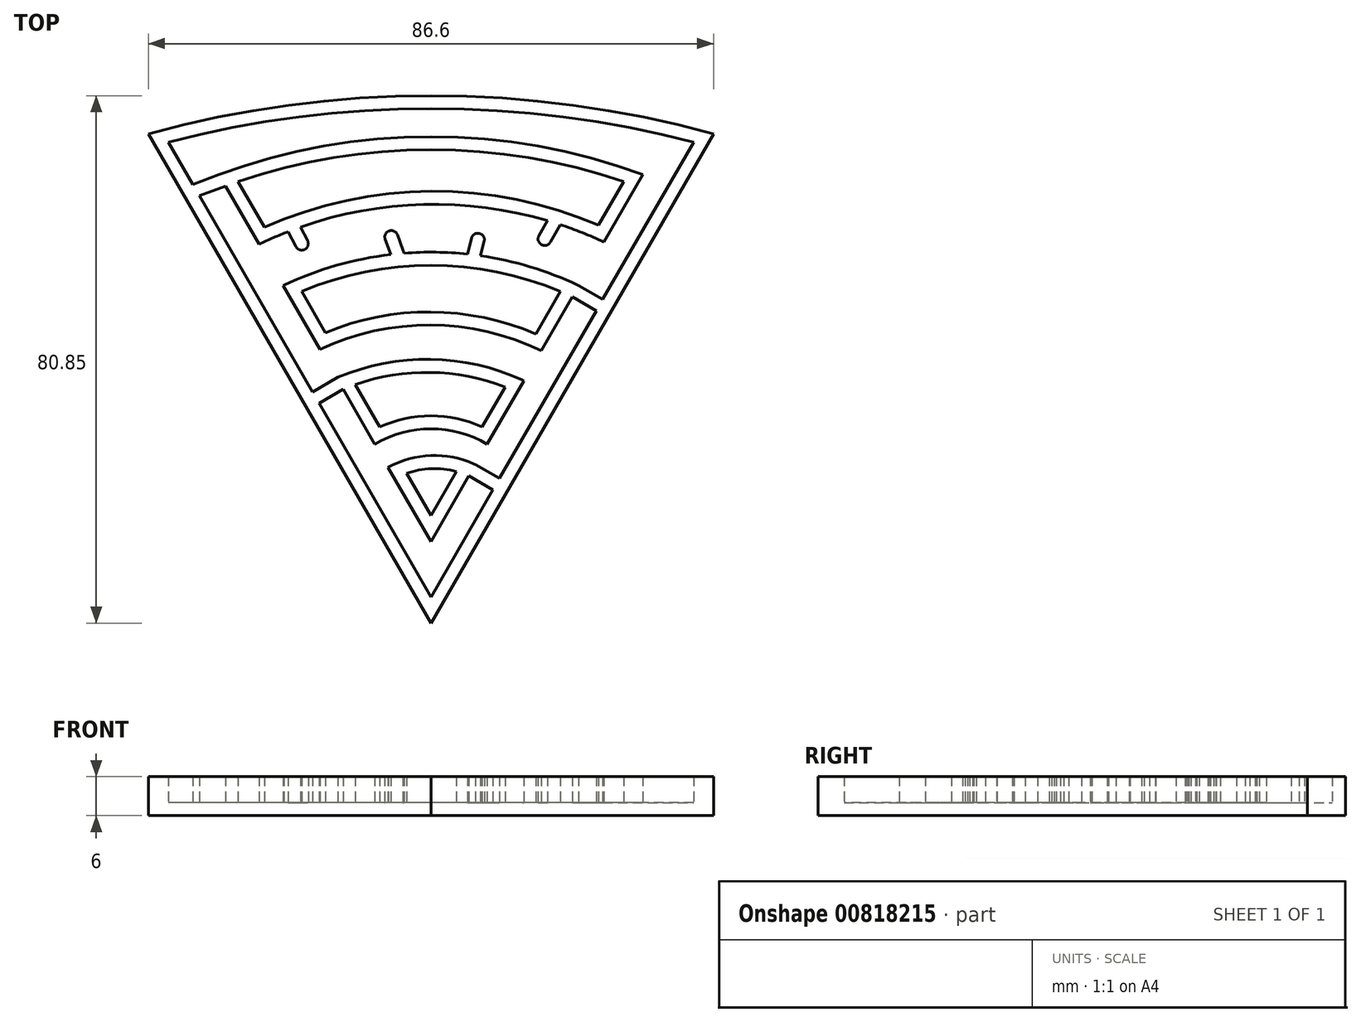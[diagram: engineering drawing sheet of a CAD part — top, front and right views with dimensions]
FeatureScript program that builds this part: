
annotation { "Feature Type Name" : "Feature", "Feature Type Description" : "" }
export const myFeature = defineFeature(function(context is Context, id is Id, definition is map)
    precondition{}
    {
        {
            var Q0;
            Q0=qCreatedBy(makeId("Top.planeOp"),FACE);
            var sketch = newSketch(context, id + "F0", { "sketchPlane" : qUnion([Q0])});
            skLineSegment(sketch, "E0.0", {"start": v(0, -50) * mm, "end": v(-43.3, 25) * mm});
            skLineSegment(sketch, "E0.2", {"start": v(43.3, 25) * mm, "end": v(0, -50) * mm});
            skLineSegment(sketch, "E1.0", {"start": v(0, -46) * mm, "end": v(-17.15, -16.3) * mm});
            skLineSegment(sketch, "E1.1", {"start": v(39.84, 23) * mm, "end": v(26.33, -0.39) * mm});
            skLineSegment(sketch, "E2.0", {"start": v(0, -37.5) * mm, "end": v(-6.57, -26.12) * mm});
            skLineSegment(sketch, "E2.2", {"start": v(32.48, 18.75) * mm, "end": v(26.51, 8.42) * mm});
            skArc(sketch, "E3", {"start": v(26.51, 8.42) * mm, "mid": v(23.2, 9.85) * mm, "end": v(19.82, 11.08) * mm});
            skArc(sketch, "E4.0", {"start": v(25.69, 10.99) * mm, "mid": v(0.06, 16.2) * mm, "end": v(-25.5, 10.67) * mm});
            skArc(sketch, "E5", {"start": v(19.82, 0.82) * mm, "mid": v(0, 4.86) * mm, "end": v(-19.82, 0.82) * mm});
            skArc(sketch, "E6.0", {"start": v(22.5, 1.8) * mm, "mid": v(15.21, 4.62) * mm, "end": v(7.58, 6.32) * mm});
            skLineSegment(sketch, "E7", {"start": v(22.5, 1.8) * mm, "end": v(22.65, 1.74) * mm});
            skLineSegment(sketch, "E8.trimOffspring", {"start": v(21.65, 0) * mm, "end": v(16.89, -8.25) * mm});
            skLineSegment(sketch, "E9", {"start": v(-22.5, 1.8) * mm, "end": v(-22.65, 1.73) * mm});
            skLineSegment(sketch, "E10.trimOffspring", {"start": v(-26.32, 8.08) * mm, "end": v(-31.46, 17) * mm});
            skArc(sketch, "E11", {"start": v(16.89, -8.25) * mm, "mid": v(-0.04, -4.3) * mm, "end": v(-17.02, -8.02) * mm});
            skArc(sketch, "E12.0", {"start": v(16.07, -5.67) * mm, "mid": v(-0.04, -2.3) * mm, "end": v(-16.18, -5.47) * mm});
            skArc(sketch, "E13", {"start": v(11.38, -13.8) * mm, "mid": v(-0.07, -11.57) * mm, "end": v(-11.59, -13.43) * mm});
            skArc(sketch, "E14.0", {"start": v(14.07, -12.75) * mm, "mid": v(-0.05, -9.57) * mm, "end": v(-14.25, -12.3) * mm});
            skLineSegment(sketch, "E15", {"start": v(14.07, -12.75) * mm, "end": v(14.24, -12.83) * mm});
            skLineSegment(sketch, "E16.trimOffspring", {"start": v(14.24, -12.83) * mm, "end": v(8.63, -22.56) * mm});
            skArc(sketch, "E17", {"start": v(8.63, -22.56) * mm, "mid": v(0, -20.22) * mm, "end": v(-8.6, -22.6) * mm});
            skArc(sketch, "E18", {"start": v(3.9, -26.75) * mm, "mid": v(0.06, -26.32) * mm, "end": v(-3.73, -27.04) * mm});
            skArc(sketch, "E19.0", {"start": v(9.64, -20.84) * mm, "mid": v(9.63, -20.83) * mm, "end": v(9.63, -20.83) * mm});
            skArc(sketch, "E20.0", {"start": v(6.63, -25.6) * mm, "mid": v(0, -24.32) * mm, "end": v(-6.52, -26.09) * mm});
            skLineSegment(sketch, "E21.trimOffspring", {"start": v(-17.02, -8.02) * mm, "end": v(-22.65, 1.73) * mm});
            skLineSegment(sketch, "E22", {"start": v(-6.52, -26.09) * mm, "end": v(-6.57, -26.12) * mm});
            skLineSegment(sketch, "E23", {"start": v(6.63, -25.6) * mm, "end": v(6.82, -25.7) * mm});
            skLineSegment(sketch, "E24.trimOffspring", {"start": v(5.82, -27.42) * mm, "end": v(0, -37.5) * mm});
            skLineSegment(sketch, "E25.trimOffspring", {"start": v(-8.6, -22.6) * mm, "end": v(-13.47, -14.17) * mm});
            skArc(sketch, "E26", {"start": v(43.3, 25) * mm, "mid": v(0, 30.85) * mm, "end": v(-43.3, 25) * mm});
            skArc(sketch, "E27", {"start": v(32.48, 18.75) * mm, "mid": v(0, 24.56) * mm, "end": v(-32.48, 18.75) * mm});
            skArc(sketch, "E28.0", {"start": v(40.26, 23.74) * mm, "mid": v(0, 28.85) * mm, "end": v(-40.26, 23.74) * mm});
            skLineSegment(sketch, "E29", {"start": v(-39.84, 23) * mm, "end": v(-40.26, 23.74) * mm});
            skLineSegment(sketch, "E30", {"start": v(39.84, 23) * mm, "end": v(40.26, 23.74) * mm});
            skLineSegment(sketch, "E31.0", {"start": v(0, -33.5) * mm, "end": v(-3.73, -27.04) * mm});
            skLineSegment(sketch, "E32.trimOffspring", {"start": v(3.9, -26.75) * mm, "end": v(0, -33.5) * mm});
            skLineSegment(sketch, "E33.0", {"start": v(-25.5, 10.67) * mm, "end": v(-29.54, 17.67) * mm});
            skLineSegment(sketch, "E34.0", {"start": v(19.82, 0.82) * mm, "end": v(16.07, -5.67) * mm});
            skLineSegment(sketch, "E35.0", {"start": v(-16.18, -5.47) * mm, "end": v(-19.82, 0.82) * mm});
            skLineSegment(sketch, "E36.0", {"start": v(-7.83, -19.94) * mm, "end": v(-11.59, -13.43) * mm});
            skLineSegment(sketch, "E37.trimOffspring", {"start": v(29.54, 17.67) * mm, "end": v(25.69, 10.99) * mm});
            skArc(sketch, "E38.trimOffspring", {"start": v(29.54, 17.67) * mm, "mid": v(0, 22.56) * mm, "end": v(-29.54, 17.67) * mm});
            skPoint(sketch, "E39.orphan", {"position": v(21.65, 0) * mm});
            skPoint(sketch, "E40.orphan", {"position": v(-21.65, 0) * mm});
            skLineSegment(sketch, "E41.trimOffspring", {"start": v(11.38, -13.8) * mm, "end": v(7.85, -19.9) * mm});
            skArc(sketch, "E42.trimOffspring", {"start": v(7.85, -19.9) * mm, "mid": v(0, -18.22) * mm, "end": v(-7.83, -19.94) * mm});
            skArc(sketch, "E43.trimOffspring", {"start": v(-9.6, -20.86) * mm, "mid": v(-9.62, -20.87) * mm, "end": v(-9.63, -20.88) * mm});
            skLineSegment(sketch, "E44", {"start": v(-14.25, -12.3) * mm, "end": v(-18.15, -14.56) * mm});
            skLineSegment(sketch, "E45", {"start": v(6.82, -25.7) * mm, "end": v(10.5, -27.82) * mm});
            skLineSegment(sketch, "E46", {"start": v(-32.48, 18.75) * mm, "end": v(-36.52, 17.25) * mm});
            skLineSegment(sketch, "E47.0", {"start": v(-31.78, 16.87) * mm, "end": v(-35.5, 15.5) * mm});
            skLineSegment(sketch, "E48", {"start": v(-31.78, 16.87) * mm, "end": v(-31.46, 17) * mm});
            skLineSegment(sketch, "E49.0", {"start": v(-13.47, -14.17) * mm, "end": v(-17.15, -16.3) * mm});
            skLineSegment(sketch, "E50.0", {"start": v(5.82, -27.42) * mm, "end": v(9.5, -29.55) * mm});
            skLineSegment(sketch, "E51.trimOffspring", {"start": v(25.33, -2.12) * mm, "end": v(10.5, -27.82) * mm});
            skLineSegment(sketch, "E52.trimOffspring", {"start": v(-36.52, 17.25) * mm, "end": v(-39.84, 23) * mm});
            skLineSegment(sketch, "E53.trimOffspring", {"start": v(-18.15, -14.56) * mm, "end": v(-35.5, 15.5) * mm});
            skLineSegment(sketch, "E54.trimOffspring", {"start": v(9.5, -29.55) * mm, "end": v(0, -46) * mm});
            skLineSegment(sketch, "E55", {"start": v(19.82, 11.08) * mm, "end": v(18.3, 8.4) * mm});
            skLineSegment(sketch, "E56", {"start": v(-6.14, 6.5) * mm, "end": v(-7, 8.83) * mm});
            skLineSegment(sketch, "E57", {"start": v(5.58, 6.57) * mm, "end": v(6.23, 9.02) * mm});
            skPoint(sketch, "E57.endSnap0", {"position": v(6.23, 7.8) * mm});
            skLineSegment(sketch, "E58.0", {"start": v(17.86, 11.7) * mm, "end": v(16.55, 9.39) * mm});
            skArc(sketch, "E59", {"start": v(16.55, 9.39) * mm, "mid": v(16.93, 8.02) * mm, "end": v(18.3, 8.4) * mm});
            skLineSegment(sketch, "E60.0", {"start": v(7.58, 6.32) * mm, "end": v(8.16, 8.51) * mm});
            skArc(sketch, "E61", {"start": v(8.16, 8.51) * mm, "mid": v(7.45, 9.73) * mm, "end": v(6.23, 9.02) * mm});
            skLineSegment(sketch, "E62.0", {"start": v(-4.27, 7.2) * mm, "end": v(-5.13, 9.52) * mm});
            skLineSegment(sketch, "E63", {"start": v(-4.27, 7.2) * mm, "end": v(-4.08, 6.7) * mm});
            skArc(sketch, "E64", {"start": v(-5.13, 9.52) * mm, "mid": v(-6.41, 10.11) * mm, "end": v(-7, 8.83) * mm});
            skArc(sketch, "E65.trimOffspring", {"start": v(-6.14, 6.5) * mm, "mid": v(-14.52, 4.82) * mm, "end": v(-22.5, 1.8) * mm});
            skArc(sketch, "E66.trimOffspring", {"start": v(5.58, 6.57) * mm, "mid": v(0.75, 6.86) * mm, "end": v(-4.08, 6.7) * mm});
            skArc(sketch, "E67.trimOffspring", {"start": v(17.86, 11.7) * mm, "mid": v(-1.15, 14.18) * mm, "end": v(-20, 10.7) * mm});
            skLineSegment(sketch, "E68", {"start": v(-21.9, 10) * mm, "end": v(-20.69, 7.7) * mm});
            skLineSegment(sketch, "E69.0", {"start": v(-20, 10.7) * mm, "end": v(-18.92, 8.63) * mm});
            skArc(sketch, "E70", {"start": v(-20.69, 7.7) * mm, "mid": v(-19.33, 7.28) * mm, "end": v(-18.92, 8.63) * mm});
            skArc(sketch, "E71.trimOffspring", {"start": v(-21.9, 10) * mm, "mid": v(-24.13, 9.09) * mm, "end": v(-26.32, 8.08) * mm});
            skLineSegment(sketch, "E72", {"start": v(21.65, 0) * mm, "end": v(25.33, -2.12) * mm});
            skLineSegment(sketch, "E73", {"start": v(22.65, 1.74) * mm, "end": v(26.33, -0.39) * mm});
            skSolve(sketch);
        }
        {
            var Q0;
            Q0=makeQuery(id+"F0.imprint","IMPRINT",FACE,{"disambiguationData":[TD([[makeQuery(id+"F0.imprint","IMPRINT",EDGE,{"derivedFrom":sQuery(id+"F0.wireOp",EDGE,"E0.0")}),-1.0]])]});
            extrude(context, id + "F1", {"entities" : qUnion([Q0]), "depth" : 6 * mm, "offsetDistance" : 25 * mm});
        }
        {
            var Q0;
            Q0=qCreatedBy(makeId("Top.planeOp"),FACE);
            var sketch = newSketch(context, id + "F2", { "sketchPlane" : qUnion([Q0])});
            skLineSegment(sketch, "E74.0", {"start": v(0, -50) * mm, "end": v(-43.3, 25) * mm});
            skLineSegment(sketch, "E75.0", {"start": v(43.3, 25) * mm, "end": v(0, -50) * mm});
            skArc(sketch, "E76.0", {"start": v(43.3, 25) * mm, "mid": v(0, 30.85) * mm, "end": v(-43.3, 25) * mm});
            skSolve(sketch);
        }
        {
            var Q0;
            Q0 = qSketchRegion(id + "F2", true);
            extrude(context, id + "F3", {"entities" : qUnion([Q0]), "operationType" : NewBodyOperationType.ADD, "depth" : 2 * mm, "offsetDistance" : 25 * mm});
        }
    });
